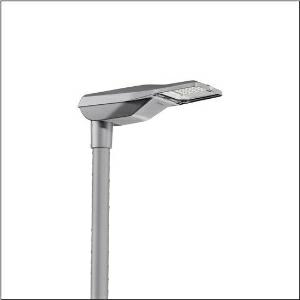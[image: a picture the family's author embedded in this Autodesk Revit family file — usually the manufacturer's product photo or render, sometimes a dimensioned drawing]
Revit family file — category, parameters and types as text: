
# Revit family: streetlight_sl_21_iq_micro___st1_0a_5xe1d31d08db_2abd
name_source: partatom
category: Lighting Fixtures
units: mm (PartAtom-declared; Revit-internal decimal feet)

## family parameters
Cut with Voids When Loaded = No
Host = Face
Light Source = No
Part Type = Normal
Room Calculation Point = No
Round Connector Dimension = Use Diameter
Shared = No

## types (1)
- --- (1 x LED, 4810 lm, 36.4 W, 3000K)
    Apparent Load = 36 VA
    CIE Flux Codes = 37 72 97 100 100
    Color Rendering = 70
    Color Temperature = 3000K
    Default Elevation = 1800 mm
    Description = Streetlight SL 21 iQ micro, mast luminaire, primary light control with lens, of PMMA, primary optical cover: cover, of toughened safety glass, transparent, light distribution: ST1.0a, light emission: direct distribution, primary light characteristic: asymmetric, installation type: post-top, side-entry, LED, High Power LED, rated luminous flux: 4.810lm, luminous efficacy: 132lm/W, light colour: 730, colour temperature: 3000K, control gear: iQ-Comfort, control: Auto-Match, Temp-Guard, Lumen-Switch, Night-Set, Smart-Wire, Light-Fading, Desk-Remote (wireless, voltage-free reading and setting of iQ features in the workshop via application-optimized NFC function/RFID function), optimised constant luminous flux control (CLO 2.0), pre-setting: linear dimming characteristic, mains connection: 220..240V, AC, 50/60Hz, start of lifetime: 36W, end of service life: 38W, reduction: 16W, luminaire housing, of diecast aluminium, powder-coated, Siteco® metallic grey (DB 702S), corrosivity category C5 mid according to DIN EN ISO 12944, please order mast flange separately, inclination adjustable: 0°, 5°, 10°, 15°, sealing non-destructively replaceable, multi-level sealing system, length: 528mm, width: 235mm, height: 110mm, mast flange for spigot size: 42mm (side-entry): 5XC10008XM4, 60/48mm (side-entry/post-top): 5XC10108XM2, 76/60mm (side-entry/post-top): 5XC10108XM1, protection rating (complete): IP66, insulation class (complete): insulation class II (safety insulation), certification: CE, ENEC, ENEC+, VDE, impact resistance: IK10, permissible operating ambient temperature for outdoor applications: -40..+50°C, standard-compliant lighting for roads and squares, packaging unit: 1 piece

Light Distribution: ST1.0a
    Height = 110 mm
    Lamp = 1 x LED
    Lamp Light Flux = 4810 lm
    Lamp Power = 36.4 W
    Lamp count = 1
    Length = 528 mm
    Luminous efficacy = 132 lm/W
    Manufacturer = Siteco
    ModVariant = No
    Model = 5XE1D31D08DB
    Number of Poles = 1
    OnlyDefault = Yes
    Power Factor = 1
    Product Name = Streetlight SL 21 iQ micro | ST1.0a
    Product group = mast luminaire | pylon top
    ProductGroupID = 6100
    Protection Class = Protection class II
    Protection Degree = IP 66
    RLX_Detail_Level = 1
    RLX_Emergency_Light_Flux = 0 lm
    RLX_Emergency_Type = 0
    RLX_Emergency_Type_DB = No
    RlxData = <blob elided: 98945 chars, md5=55063771>
    Socket = socket
    Standby Power = 0 W
    System Light Flux = 4810 lm
    System Power = 36 W
    Type Comments = factory setting: luminous flux: 100 % | dim-lin: 254 | 715 mA
    Type Image = l_1006881.jpg
    URL = http://relux.com
    VarID = @adj_177505
    Voltage = 0 V
    Weight = 0.00 kg
    Width = 235 mm

## geometry (parser evidence)
native form markers: Blend x4, Sweep x10
no freeform markers — native parametric forms only
